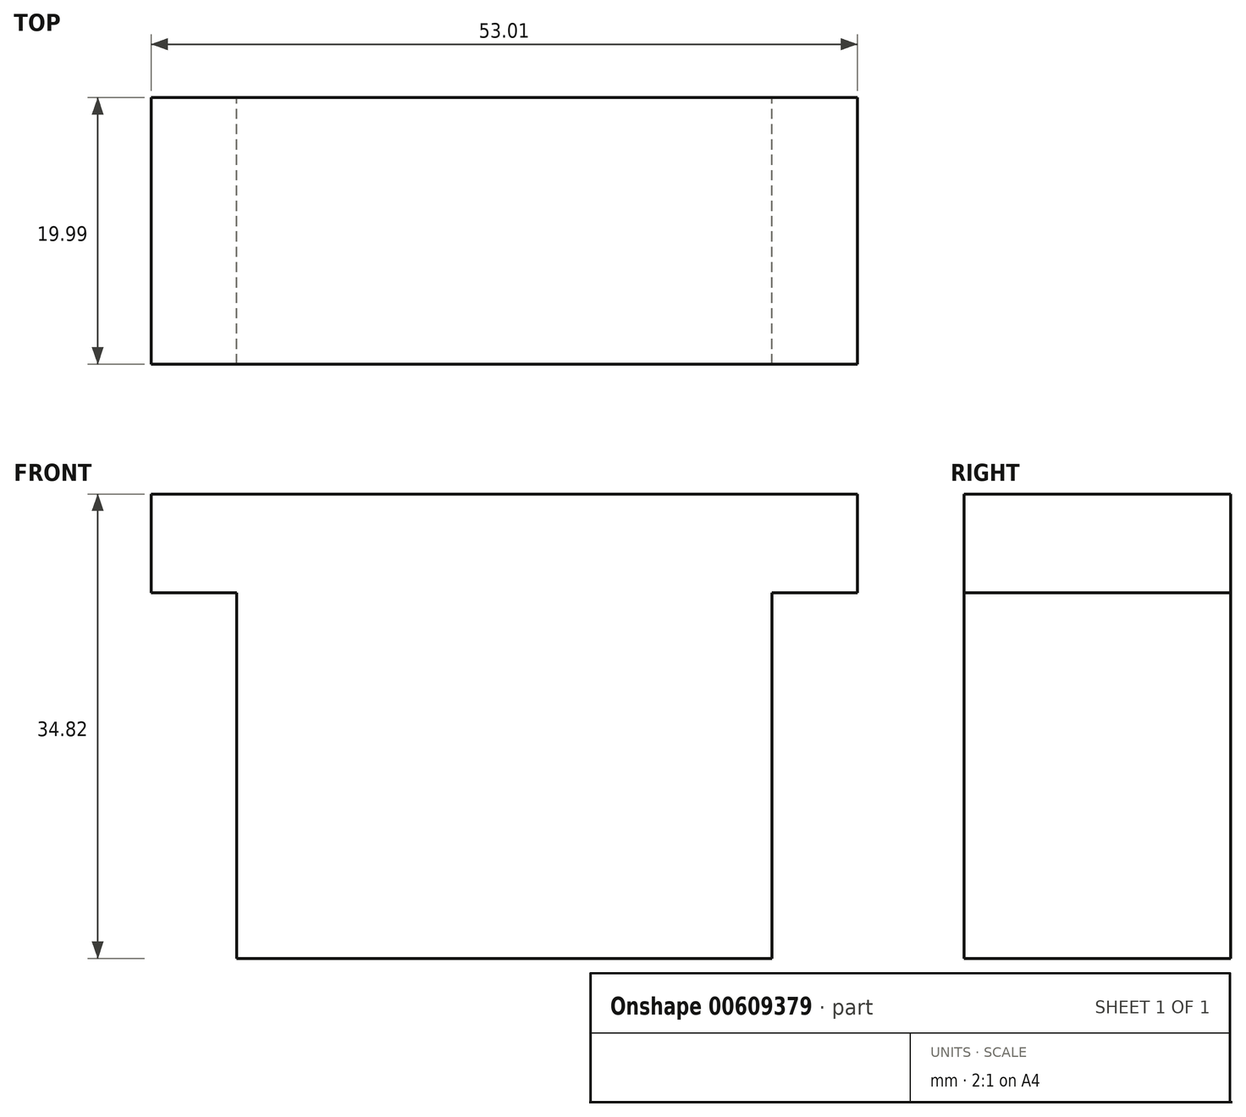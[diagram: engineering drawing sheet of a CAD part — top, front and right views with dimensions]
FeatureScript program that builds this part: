
annotation { "Feature Type Name" : "Feature", "Feature Type Description" : "" }
export const myFeature = defineFeature(function(context is Context, id is Id, definition is map)
    precondition{}
    {
        {
            var Q0;
            Q0=qCreatedBy(makeId("Front.planeOp"),FACE);
            var sketch = newSketch(context, id + "F0", { "sketchPlane" : qUnion([Q0])});
            skLineSegment(sketch, "E0", {"start": v(0, 0) * mm, "end": v(-40.16, 0) * mm});
            skLineSegment(sketch, "E1", {"start": v(-40.16, 0) * mm, "end": v(-40.16, 27.43) * mm});
            skLineSegment(sketch, "E2", {"start": v(-40.16, 27.43) * mm, "end": v(-46.58, 27.43) * mm});
            skLineSegment(sketch, "E3", {"start": v(-46.58, 27.43) * mm, "end": v(-46.58, 34.82) * mm});
            skLineSegment(sketch, "E4", {"start": v(-46.58, 34.82) * mm, "end": v(6.43, 34.82) * mm});
            skLineSegment(sketch, "E5", {"start": v(6.43, 34.82) * mm, "end": v(6.43, 27.43) * mm});
            skLineSegment(sketch, "E6", {"start": v(6.43, 27.43) * mm, "end": v(0, 27.43) * mm});
            skLineSegment(sketch, "E7", {"start": v(0, 27.43) * mm, "end": v(0, 0) * mm});
            skSolve(sketch);
        }
        {
            var Q0;
            Q0 = qSketchRegion(id + "F0", true);
            extrude(context, id + "F1", {"entities" : qUnion([Q0]), "depth" : 19.99 * mm, "offsetDistance" : 25.4 * mm});
        }
    });
